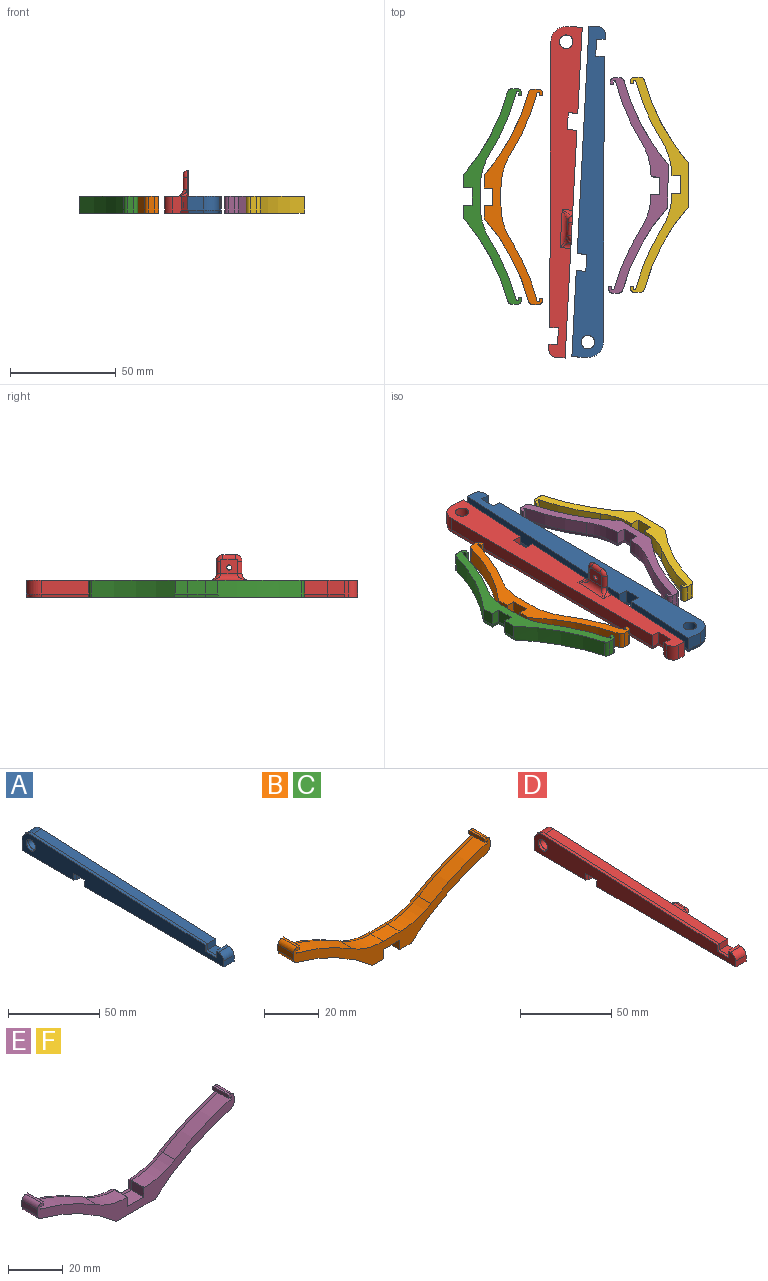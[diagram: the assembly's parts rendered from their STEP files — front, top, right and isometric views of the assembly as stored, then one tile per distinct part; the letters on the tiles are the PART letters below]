
ASSEMBLY  parts=6 mates=4
PART A: 29 faces, bbox 8x156.2x14.4 mm
  f0: plane 8x6.5mm, normal (0,0,-1), area 52mm2, adj f1,f13,f14,f22
  f1: plane 6.5x4.5mm, normal (0,-1,0), area 29.3mm2, adj f0,f2,f14,f24
  f2: plane 40.61x6.5mm, normal (0,0,-1), area 263.9mm2, adj f1,f3,f14,f26
  f3: plane 7.21x6.5mm, normal (0,1,0), area 46.8mm2, adj f2,f4,f14,f27
  f4: cylinder r=7.21mm len=7.55mm, axis (-1,0,0), area 75.8mm2, adj f3,f5,f14,f25
  f5: plane 134.66x6.5mm, normal (0,-0.05,1), area 876.3mm2, adj f4,f6,f14,f23
  f6: plane 6.5x4.1mm, normal (0,-1,0), area 26.7mm2, adj f5,f7,f14,f21
  f7: plane 8x6.5mm, normal (0,0,1), area 52mm2, adj f6,f8,f14,f19
  f8: plane 6.5x4.1mm, normal (0,1,0), area 26.7mm2, adj f7,f9,f14,f17
  f9: plane 8x2mm, normal (0,0,1), area 15.7mm2, adj f8,f14,f15,f16,f17
  f10: plane 8x4mm, normal (0,-1,0), area 31.7mm2, adj f11,f14,f15,f16,f18
  f11: plane 107.6x6.5mm, normal (0,0,-1), area 699.4mm2, adj f10,f13,f14,f18
  f12: cylinder r=3.21mm len=6.5mm, axis (-1,0,0), area 131mm2, adj f14,f28
  f13: plane 6.5x4.5mm, normal (0,1,0), area 29.3mm2, adj f0,f11,f14,f20
  f14: plane 156.21x14.41mm, normal (1,0,0), area 1613.6mm2, adj f0,f1,f2,f3,f4,f5,f6,f7
  f15: plane 155.86x13.71mm, normal (-1,0,0), area 1489mm2, adj f9,f10,f16,f17,f18,f19,f20,f21
  f16: cylinder r=4mm len=8mm, axis (-1,0,0), area 50.3mm2, adj f9,f10,f14,f15
  f17: plane 4.45x1.5mm, normal (-0.23,0.97,0), area 6.6mm2, adj f8,f9,f15,f19
  f18: plane 107.6x1.5mm, normal (-0.23,0,-0.97), area 165.5mm2, adj f10,f11,f15,f20
  f19: plane 8.7x1.5mm, normal (-0.23,0,0.97), area 12.9mm2, adj f7,f15,f17,f21
  f20: plane 4.85x1.5mm, normal (-0.23,0.97,0), area 6.9mm2, adj f13,f15,f18,f22
  f21: plane 4.45x1.5mm, normal (-0.23,-0.97,0), area 6.3mm2, adj f6,f15,f19,f23
  f22: plane 8.7x1.5mm, normal (-0.23,0,-0.97), area 12.9mm2, adj f0,f15,f20,f24
  f23: plane 134.67x6.74mm, normal (-0.23,-0.05,0.97), area 207.4mm2, adj f5,f15,f21,f25
  f24: plane 4.85x1.5mm, normal (-0.23,-0.97,0), area 6.9mm2, adj f1,f15,f22,f26
  f25: cone r=7.21mm half-angle=13.1deg, axis (1,0,0), area 17.5mm2, adj f4,f15,f23,f27
  f26: plane 40.61x1.5mm, normal (-0.23,0,-0.97), area 62mm2, adj f2,f15,f24,f27
  f27: plane 7.21x1.5mm, normal (-0.23,0.97,0), area 10.8mm2, adj f3,f15,f25,f26
  f28: cone r=3.56mm half-angle=13.1deg, axis (-1,0,0), area 32.7mm2, adj f12,f15
PART B: 38 faces, bbox 101.6x8x27.6 mm
  f0: plane 6.5x5.85mm, normal (0,0,-1), area 38mm2, adj f1,f19,f20,f33
  f1: cylinder r=100mm len=39.33mm, axis (0,1,0), area 359.3mm2, adj f0,f20,f21,f22,f33
  f2: plane 8x2.7mm, normal (1,0,0), area 21.6mm2, adj f20,f21,f22,f23
  f3: plane 8x1mm, normal (0,0,1), area 8mm2, adj f4,f20,f21,f23
  f4: plane 8x1.5mm, normal (-1,0,0), area 12mm2, adj f3,f5,f20,f21
  f5: plane 8x1.5mm, normal (0,0,-1), area 12mm2, adj f4,f6,f20,f21
  f6: plane 8x1.36mm, normal (-1,0,0), area 8.3mm2, adj f5,f7,f20,f21,f28
  f7: cylinder r=104mm len=29.01mm, axis (0,1,0), area 206.3mm2, adj f6,f20,f26,f28
  f8: plane 8.66x6.5mm, normal (0,0,1), area 56.3mm2, adj f20,f26,f27,f30
  f9: cylinder r=104mm len=29.01mm, axis (0,1,0), area 206.3mm2, adj f10,f20,f27,f32
  f10: plane 8x1.36mm, normal (1,0,0), area 8.3mm2, adj f9,f11,f20,f21,f32
  f11: plane 8x1.5mm, normal (0,0,-1), area 12mm2, adj f10,f12,f20,f21
  f12: plane 8x1.5mm, normal (1,0,0), area 12mm2, adj f11,f13,f20,f21
  f13: plane 8x1mm, normal (0,0,1), area 8mm2, adj f12,f20,f21,f24
  f14: plane 8x2.7mm, normal (-1,0,0), area 21.6mm2, adj f20,f21,f24,f25
  f15: cylinder r=100mm len=39.33mm, axis (0,1,0), area 359.3mm2, adj f16,f20,f21,f25,f35
  f16: plane 6.5x5.85mm, normal (0,0,-1), area 38mm2, adj f15,f17,f20,f35
  f17: plane 6.5x4.2mm, normal (1,0,0), area 27.3mm2, adj f16,f18,f20,f37
  f18: plane 8.3x6.5mm, normal (0,0,-1), area 54mm2, adj f17,f19,f20,f36
  f19: plane 6.5x4.2mm, normal (-1,0,0), area 27.3mm2, adj f0,f18,f20,f34
  f20: plane 101.6x27.64mm, normal (0,-1,0), area 528.9mm2, adj f0,f1,f2,f3,f4,f5,f6,f7
  f21: plane 101.6x27.29mm, normal (0,1,0), area 481.8mm2, adj f1,f2,f3,f4,f5,f6,f10,f11
  f22: cylinder r=2mm len=8mm, axis (0,1,0), area 20.9mm2, adj f1,f2,f20,f21
  f23: cylinder r=2mm len=8mm, axis (0,1,0), area 25.1mm2, adj f2,f3,f20,f21
  f24: cylinder r=2mm len=8mm, axis (0,1,0), area 25.1mm2, adj f13,f14,f20,f21
  f25: cylinder r=2mm len=8mm, axis (0,1,0), area 20.9mm2, adj f14,f15,f20,f21
  f26: cylinder r=30mm len=15.96mm, axis (0,1,0), area 109.4mm2, adj f7,f8,f20,f29
  f27: cylinder r=30mm len=15.96mm, axis (0,1,0), area 109.4mm2, adj f8,f9,f20,f31
  f28: cone r=103.65mm half-angle=13.1deg, axis (0,-1,0), area 48.7mm2, adj f6,f7,f21,f29
  f29: cone r=30.35mm half-angle=13.1deg, axis (0,1,0), area 26.1mm2, adj f21,f26,f28,f30
  f30: plane 8.66x1.5mm, normal (0,0.23,0.97), area 13.3mm2, adj f8,f21,f29,f31
  f31: cone r=30.35mm half-angle=13.1deg, axis (0,1,0), area 26.1mm2, adj f21,f27,f30,f32
  f32: cone r=104mm half-angle=13.1deg, axis (0,-1,0), area 48.7mm2, adj f9,f10,f21,f31
  f33: plane 6.26x1.5mm, normal (0,0.23,-0.97), area 9.1mm2, adj f0,f1,f21,f34
  f34: plane 4.55x1.5mm, normal (-0.97,0.23,0), area 6.5mm2, adj f19,f21,f33,f36
  f35: plane 6.26x1.5mm, normal (0,0.23,-0.97), area 9.1mm2, adj f15,f16,f21,f37
  f36: plane 9x1.5mm, normal (0,0.23,-0.97), area 13.3mm2, adj f18,f21,f34,f37
  f37: plane 4.55x1.5mm, normal (0.97,0.23,0), area 6.5mm2, adj f17,f21,f35,f36
PART C: same geometry as B
PART D: 43 faces, bbox 20x156.2x14.4 mm
  f0: plane 156.21x14.41mm, normal (1,0,0), area 1523.6mm2, adj f1,f2,f3,f4,f5,f6,f7,f8
  f1: plane 8x6.5mm, normal (0,0,-1), area 52mm2, adj f0,f2,f14,f36
  f2: plane 6.5x4.5mm, normal (0,-1,0), area 29.2mm2, adj f0,f1,f3,f38
  f3: plane 40.61x6.5mm, normal (0,0,-1), area 263.9mm2, adj f0,f2,f4,f40
  f4: plane 7.21x6.5mm, normal (0,1,0), area 46.8mm2, adj f0,f3,f5,f41
  f5: cylinder r=7.21mm len=7.55mm, axis (-1,0,0), area 75.8mm2, adj f0,f4,f6,f39
  f6: plane 134.66x6.5mm, normal (0,-0.05,1), area 876.3mm2, adj f0,f5,f7,f37
  f7: plane 6.5x4.1mm, normal (0,-1,0), area 26.7mm2, adj f0,f6,f8,f35
  f8: plane 8x6.5mm, normal (0,0,1), area 52mm2, adj f0,f7,f9,f33
  f9: plane 6.5x4.1mm, normal (0,1,0), area 26.7mm2, adj f0,f8,f10,f31
  f10: plane 8x2mm, normal (0,0,1), area 15.7mm2, adj f0,f9,f15,f16,f31
  f11: plane 8x4mm, normal (0,-1,0), area 31.7mm2, adj f0,f12,f15,f16,f32
  f12: plane 107.6x18.5mm, normal (0,0,-1), area 834.1mm2, adj f0,f11,f14,f18,f20,f22,f23,f24
  f13: cylinder r=3.21mm len=6.5mm, axis (-1,0,0), area 131mm2, adj f0,f42
  f14: plane 6.5x4.5mm, normal (0,1,0), area 29.2mm2, adj f0,f1,f12,f34
  f15: plane 155.86x13.71mm, normal (-1,0,0), area 1489mm2, adj f10,f11,f16,f31,f32,f33,f34,f35
  f16: cylinder r=4mm len=8mm, axis (-1,0,0), area 50.3mm2, adj f0,f10,f11,f15
  f17: plane 8x7mm, normal (0,0,1), area 50.9mm2, adj f19,f22,f23,f24,f25,f26,f30
  f18: cylinder r=3mm len=5mm, axis (0,0,1), area 8.6mm2, adj f0,f12,f27
  f19: cylinder r=3mm len=18mm, axis (0,-1,0), area 54.8mm2, adj f0,f17,f21,f27
  f20: cylinder r=3mm len=5mm, axis (0,0,-1), area 8.6mm2, adj f0,f12,f21
  f21: bspline ~5x5mm, area 11mm2, adj f19,f20,f22
  f22: cylinder r=2mm len=6mm, axis (1,0,0), area 18.8mm2, adj f12,f17,f21,f23
  f23: torus R=1mm, axis (0,0,1), area 11.2mm2, adj f12,f17,f22,f24
  f24: cylinder r=2mm len=6mm, axis (0,1,0), area 18.8mm2, adj f12,f17,f23,f25
  f25: torus R=1mm, axis (0,0,1), area 11.2mm2, adj f12,f17,f24,f26
  f26: cylinder r=2mm len=6mm, axis (-1,0,0), area 18.8mm2, adj f12,f17,f25,f27
  f27: bspline ~5x5mm, area 11mm2, adj f18,f19,f26
  f28: cylinder r=1.22mm len=2.44mm, axis (0,0,1), area 15.3mm2, adj f12,f29
  f29: plane 2.44x2.44mm, normal (0,0,-1), area 4.7mm2, adj f28
  f30: cylinder r=1.22mm len=2.44mm, axis (0,0,1), area 15.3mm2, adj f12,f17
  f31: plane 4.45x1.5mm, normal (-0.23,0.97,0), area 6.6mm2, adj f9,f10,f15,f33
  f32: plane 107.6x1.5mm, normal (-0.23,0,-0.97), area 165.5mm2, adj f11,f12,f15,f34
  f33: plane 8.7x1.5mm, normal (-0.23,0,0.97), area 12.9mm2, adj f8,f15,f31,f35
  f34: plane 4.85x1.5mm, normal (-0.23,0.97,0), area 6.9mm2, adj f14,f15,f32,f36
  f35: plane 4.45x1.5mm, normal (-0.23,-0.97,0), area 6.3mm2, adj f7,f15,f33,f37
  f36: plane 8.7x1.5mm, normal (-0.23,0,-0.97), area 12.9mm2, adj f1,f15,f34,f38
  f37: plane 134.67x6.74mm, normal (-0.23,-0.05,0.97), area 207.4mm2, adj f6,f15,f35,f39
  f38: plane 4.85x1.5mm, normal (-0.23,-0.97,0), area 6.9mm2, adj f2,f15,f36,f40
  f39: cone r=7.21mm half-angle=13.1deg, axis (1,0,0), area 17.5mm2, adj f5,f15,f37,f41
  f40: plane 40.61x1.5mm, normal (-0.23,0,-0.97), area 62mm2, adj f3,f15,f38,f41
  f41: plane 7.21x1.5mm, normal (-0.23,0.97,0), area 10.8mm2, adj f4,f15,f39,f40
  f42: cone r=3.56mm half-angle=13.1deg, axis (-1,0,0), area 32.7mm2, adj f13,f15
PART E: 38 faces, bbox 101.6x8x27.6 mm
  f0: plane 8x1mm, normal (0,0,1), area 8mm2, adj f19,f20,f21,f22
  f1: plane 8x2.7mm, normal (-1,0,0), area 21.6mm2, adj f20,f21,f22,f23
  f2: cylinder r=100mm len=39.33mm, axis (0,1,0), area 359.3mm2, adj f3,f20,f21,f23,f37
  f3: plane 20x6.5mm, normal (0,0,-1), area 130mm2, adj f2,f4,f20,f37
  f4: cylinder r=100mm len=39.33mm, axis (0,1,0), area 359.3mm2, adj f3,f20,f21,f24,f37
  f5: plane 8x2.7mm, normal (1,0,0), area 21.6mm2, adj f20,f21,f24,f25
  f6: plane 8x1mm, normal (0,0,1), area 8mm2, adj f7,f20,f21,f25
  f7: plane 8x1.5mm, normal (-1,0,0), area 12mm2, adj f6,f8,f20,f21
  f8: plane 8x1.5mm, normal (0,0,-1), area 12mm2, adj f7,f9,f20,f21
  f9: plane 8x1.36mm, normal (-1,0,0), area 8.3mm2, adj f8,f10,f20,f21,f36
  f10: cylinder r=104mm len=29.01mm, axis (0,1,0), area 206.3mm2, adj f9,f20,f26,f36
  f11: plane 6.5x0.18mm, normal (0,0,1), area 1.2mm2, adj f12,f20,f26,f33
  f12: plane 6.5x4.2mm, normal (-1,0,0), area 27.3mm2, adj f11,f13,f20,f34
  f13: plane 8.3x6.5mm, normal (0,0,1), area 53.9mm2, adj f12,f14,f20,f32
  f14: plane 6.5x4.2mm, normal (1,0,0), area 27.3mm2, adj f13,f15,f20,f31
  f15: plane 6.5x0.18mm, normal (0,0,1), area 1.2mm2, adj f14,f20,f27,f29
  f16: cylinder r=104mm len=29.01mm, axis (0,1,0), area 206.3mm2, adj f17,f20,f27,f28
  f17: plane 8x1.36mm, normal (1,0,0), area 8.3mm2, adj f16,f18,f20,f21,f28
  f18: plane 8x1.5mm, normal (0,0,-1), area 12mm2, adj f17,f19,f20,f21
  f19: plane 8x1.5mm, normal (1,0,0), area 12mm2, adj f0,f18,f20,f21
  f20: plane 101.6x27.64mm, normal (0,-1,0), area 528.9mm2, adj f0,f1,f2,f3,f4,f5,f6,f7
  f21: plane 101.6x27.29mm, normal (0,1,0), area 481.8mm2, adj f0,f1,f2,f4,f5,f6,f7,f8
  f22: cylinder r=2mm len=8mm, axis (0,1,0), area 25.1mm2, adj f0,f1,f20,f21
  f23: cylinder r=2mm len=8mm, axis (0,1,0), area 20.9mm2, adj f1,f2,f20,f21
  f24: cylinder r=2mm len=8mm, axis (0,1,0), area 20.9mm2, adj f4,f5,f20,f21
  f25: cylinder r=2mm len=8mm, axis (0,1,0), area 25.1mm2, adj f5,f6,f20,f21
  f26: cylinder r=30mm len=15.96mm, axis (0,1,0), area 109.4mm2, adj f10,f11,f20,f35
  f27: cylinder r=30mm len=15.96mm, axis (0,1,0), area 109.4mm2, adj f15,f16,f20,f30
  f28: cone r=104mm half-angle=13.1deg, axis (0,-1,0), area 48.7mm2, adj f16,f17,f21,f30
  f29: plane 0.78x0.18mm, normal (0,0.23,0.97), area 0.1mm2, adj f15,f30,f31
  f30: cone r=30.35mm half-angle=13.1deg, axis (0,1,0), area 26mm2, adj f21,f27,f28,f29,f31
  f31: plane 4.55x1.5mm, normal (0.97,0.23,0), area 6.5mm2, adj f14,f21,f29,f30,f32
  f32: plane 9x1.5mm, normal (0,0.23,0.97), area 13.3mm2, adj f13,f21,f31,f34
  f33: plane 0.78x0.18mm, normal (0,0.23,0.97), area 0.1mm2, adj f11,f34,f35
  f34: plane 4.55x1.5mm, normal (-0.97,0.23,0), area 6.5mm2, adj f12,f21,f32,f33,f35
  f35: cone r=30.35mm half-angle=13.1deg, axis (0,1,0), area 26mm2, adj f21,f26,f33,f34,f36
  f36: cone r=104mm half-angle=13.1deg, axis (0,-1,0), area 48.7mm2, adj f9,f10,f21,f35
  f37: plane 20.81x1.5mm, normal (0,0.23,-0.97), area 31.4mm2, adj f2,f3,f4,f21
PART F: same geometry as E
PLACE A rot(axis=(0.71,-0.02,0.71),177.9deg) t=(-25.54,-71.11,-76.3)mm
PLACE B rot(axis=(-0.58,0.58,-0.58),120deg) t=(-67.97,-14.88,-101.7)mm
PLACE C rot(axis=(-0.58,0.58,-0.58),120deg) t=(-77.81,-14.71,-101.7)mm
PLACE D rot(axis=(-0.03,-1,-0.03),90deg) t=(-22.63,45.91,25.3)mm
PLACE E rot(axis=(-0.58,-0.58,0.58),119.7deg) t=(18.82,-9.72,-0.1)mm
PLACE F rot(axis=(-0.58,-0.58,0.58),120deg) t=(28.67,-9.19,-0.1)mm
MATE planar C.f21 <-> E.f21  axis (0,0,-1) through (-77.46,-25.12,21.3)mm
MATE planar F.f21 <-> B.f21  axis (0,0,-1) through (16.84,-9.19,21.3)mm
MATE planar E.f21 <-> D.f15  axis (0,0,-1) through (15.33,-14.2,21.3)mm
MATE planar F.f21 <-> A.f15  axis (0,0,-1) through (28.32,-19.59,21.3)mm
